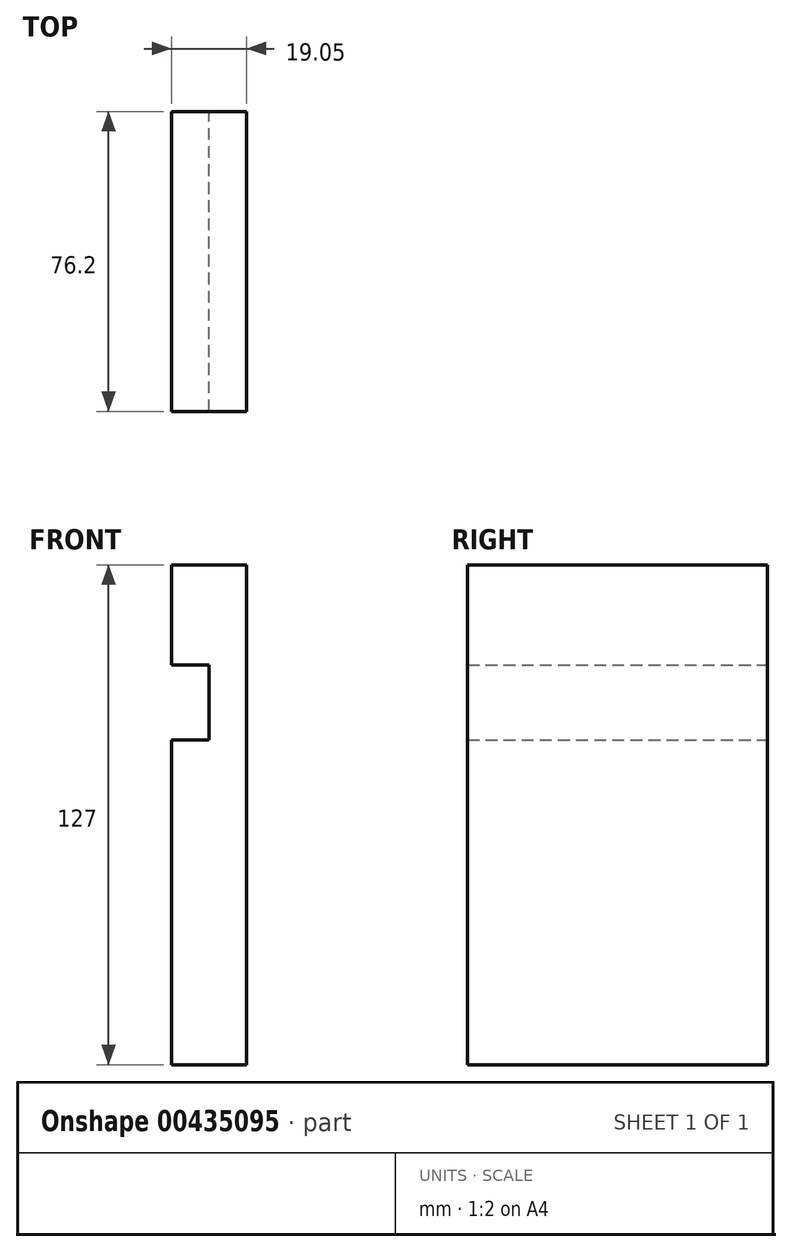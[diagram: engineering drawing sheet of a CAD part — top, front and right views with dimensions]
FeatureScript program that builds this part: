
annotation { "Feature Type Name" : "Feature", "Feature Type Description" : "" }
export const myFeature = defineFeature(function(context is Context, id is Id, definition is map)
    precondition{}
    {
        {
            var Q0;
            Q0=qCreatedBy(makeId("Front.planeOp"),FACE);
            var sketch = newSketch(context, id + "F0", { "sketchPlane" : qUnion([Q0])});
            skLineSegment(sketch, "E0", {"start": v(37.95, -67.03) * mm, "end": v(37.95, 59.97) * mm});
            skLineSegment(sketch, "E1", {"start": v(37.95, 59.97) * mm, "end": v(18.9, 59.97) * mm});
            skLineSegment(sketch, "E2", {"start": v(18.9, 59.97) * mm, "end": v(18.9, 34.57) * mm});
            skLineSegment(sketch, "E3", {"start": v(18.9, 34.57) * mm, "end": v(28.43, 34.57) * mm});
            skLineSegment(sketch, "E4", {"start": v(28.43, 34.57) * mm, "end": v(28.43, 15.52) * mm});
            skLineSegment(sketch, "E5", {"start": v(28.43, 15.52) * mm, "end": v(18.9, 15.52) * mm});
            skLineSegment(sketch, "E6", {"start": v(18.9, 15.52) * mm, "end": v(18.9, -67.03) * mm});
            skLineSegment(sketch, "E7", {"start": v(18.9, -67.03) * mm, "end": v(37.95, -67.03) * mm});
            skSolve(sketch);
        }
        {
            var Q0;
            Q0 = qSketchRegion(id + "F0", true);
            extrude(context, id + "F1", {"entities" : qUnion([Q0]), "depth" : 76.2 * mm});
        }
    });
